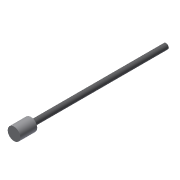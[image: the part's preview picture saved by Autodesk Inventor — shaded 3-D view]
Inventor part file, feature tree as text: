
AUTODESK INVENTOR PART (.ipt)
format: ipt  version: 2019.4 (Build 234330000, 330)  size: 89,088 bytes
history: native  units: mm
features: extrude x3, sketch x3, thread x1, projected_geometry x1
ambient origin geometry x8: Origin, YZ Plane, XZ Plane, XY Plane, X Axis, Y Axis, Z Axis, Center Point
bodies: Solid1 (feature_tree)
feature tree (8):
  extrude  "Extrusion1"  Depth=350.0mm TaperAngle=0.0deg
  extrude  "Extrusion2"  Depth=25.0mm TaperAngle=0.0deg
  thread  "Thread1"  [1 undecoded]
  extrude  "Extrusion3"  [1 undecoded]
  sketch  "Sketch1"  dims[d0=8.0mm d1=350.0mm d2=0.0mm]
  sketch  "Sketch2"  dims[d3=18.8mm d4=25.0mm d5=0.0mm d6=10.0mm d7=0.0mm]
  sketch  "Sketch3"  dims[d8=120.0mm d9=0.0mm]
  projected_geometry  "Projected Loop1"
note: 2 required parameter values undecoded (feature->parameter linkage not recoverable at this tier; creation-order binding heuristic only, values carry confidence <= 0.55)
